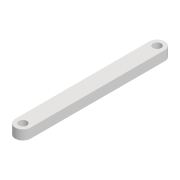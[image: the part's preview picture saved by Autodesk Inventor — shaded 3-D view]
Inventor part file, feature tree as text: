
AUTODESK INVENTOR PART (.ipt)
format: ipt  version: 2022 (Build 260153000, 153)  size: 88,064 bytes
history: native  units: mm
features: extrude x1, sketch x1
ambient origin geometry x8: Origin, YZ Plane, XZ Plane, XY Plane, X Axis, Y Axis, Z Axis, Center Point
bodies: Solid1 (feature_tree)
feature tree (2):
  extrude  "Extrusion1"  Depth=8.0mm
  sketch  "Sketch1"  dims[d0=68.0mm d1=8.0mm d2=4.2mm d3=4.2mm d4=5.0mm d5=0.0mm]
